# Revit family: IS_iLifeA_T4518_BIM_NL
name_source: partatom
category: Plumbing Fixtures
units: mm (PartAtom-declared; Revit-internal decimal feet)

## family parameters
Always vertical = No
Cut with Voids When Loaded = No
OmniClass Number = 23.45.05.14.14
OmniClass Title = Sinks/Lavatories
Part Type = Normal
Room Calculation Point = No
Round Connector Dimension = Use Diameter
Shared = No
Work Plane-Based = No

## types (1)
- T451801 - I.life A pedestal white - White
    Accessories = https://www.idealstandard.nl
    Afmetingen = 168 x 705 x 185mm
    AfstandsEenheid = Millimeter
    Afwerking = Weiß
    AreaMeasurement = internal
    AreaUnits = Millimeter
    Artikelnummer = T451801
    Artikelomschrijving = I.life A sokkel wit - Wit
    Artikelreferentie = I.life A pedestal white
    Auteur = Ideal Standard
    BIMObjectName = IS_IdealStandard_Pedestalwashbasins_I.life_T4518
    BIMobject category = Other Sanitary
    BIMobject category code = sanitary-sanitary-other
    BIMobject main category = Sanitary
    BIMobject main category code = sanitary
    BarCode = 8014140485865
    Beschrijvinggarantie = Herstellergarantie
    Bestanddelen = Sockel weiß
    BimObjectNaam = IS_IdealStandard_Pedestalwashbasins_I.life_T4518
    Brand url = https://www.idealstandard.nl
    Breedte = 0
    BrutoGewicht = 0
    Color = Weiß
    ConnectionType = Plumbing
    Cost = 0 $
    CurrencyUnit = €
    CurrentRevision = 1
    Date of publishing = 28/06/2021
    Description = I.life A sokkel wit - Wit
    Diepte = 0 mm  [stored 0 ft]
    DrainSize = 0 mm  [stored 0 ft]
    DurationUnit = Years
    DuurEenheid = Jaar
    Edition number = 1
    Eigenschappen = Sockel weiß
    Features = Sockel weiß
    Finish = Weiß
    GTIN code = https://8014140485865
    Garantieonderdelen = 5
    Garantieunits = Jaar
    GrootteAfvoergat = 0
    Help = https://www.idealstandard.nl
    Hoogte = 705.0001
    Hulp = https://www.idealstandard.nl
    IFC Classification = Sanitary Terminal
    IfcExportAs = IfcSanitaryTerminalType
    IfcExportType = PEDESTAL
    Installatieinstructies = https://www.idealstandard.nl
    Installation instructions = https://www.idealstandard.nl
    InstallationInstructions = https://www.idealstandard.nl
    Kleur = Weiß
    Lengte = 168 mm
    LinearUnits = millimeter
    MainColor = Weiß
    MaintenanceInformation = https://www.idealstandard.nl
    Manufacturer = Ideal Standard
    Manufacturer name = Ideal Standard
    ManufacturerURL = https://www.idealstandard.nl
    Material = Vitrous China
    Material main = Vitrous China
    Merk = Ideal Standard
    Model = T451801
    ModelNumber = T451801
    ModelReference = I.life A pedestal white
    Montageinstuctie = Wandhangende wastafels
    NBS Reference Code = 35-79-64
    NBS Reference Description = Pedestal Wash Basins
    Name = Pedestalwashbasins_I.life_T4518_IdealStandard
    NettWeight = 11.74
    Nettogewicht = 0
    NominalDepth = 168 mm
    NominalHeight = 705 mm
    NominalWidth = 185 mm
    Normen = Pedestalwashbasins_I.life_T4518_IdealStandard
    OmniClass Code = 23-21 25 23 15
    OmniClass Description = Pedestals
    Ophangingwastafel = Wandhangende wastafels
    OppervlakteEenheid = millimeter
    Overloop = 0 mm  [stored 0 ft]
    Product Guid = 088b959a-6ddd-48dc-a18d-73adf966bce9
    Product SKU = T4518
    Product certification = https://www.idealstandard.nl
    Product data url = https://bimobject.com
    Product family = I.life
    Product group = Pedestal
    Product name = I.life A pedestal white
    Product url = https://www.idealstandard.nl
    ProductInformation = https://www.idealstandard.nl
    ProductSoort = Wastafel
    Productinformatie = https://www.idealstandard.nl
    QR code = http://bimobject.com
    Referentie = I.life A pedestal white
    Revisie = 1
    Shape = sculpture
    Size = 168 x 705 x 185mm
    Space = Internal
    SpareParts = https://www.idealstandard.nl
    Technical description = https://www.idealstandard.nl
    Telefoonnummer = 077 355 08 08
    Typeconnectie = loodgieter
    Typewastafel = wandhangende wastafel
    URL = https://https:
    Uniclass 1.4 Code = L8443
    Uniclass 1.4 Description = Stands, pedestals
    Uniclass 2.0 Code = PR-35-79-64
    Uniclass 2.0 Description = Pedestal Wash Basins
    Uniclass 2015 Code = Pr_40_20_96_63
    Uniclass 2015 Name = Pedestal wash basins
    Uniclass2015Beschrijving = Pedestal washbasins
    Uniclass2015Code = Pr_40_20_96_63
    Uniclass2015Referentie = Pr_40_20_96_63
    Uniclass2015Title = Pedestal washbasins
    Uniclass2015Version = v1.20
    Urlproducent = https://https:
    ValutaEenheid = €
    Versie = 1
    Version = 1
    Vervangingskosten = 0
    VolumeUnits = liters
    Volumeunits = liters
    Vorm = beeldhouwwerk
    WRASURL = https://www.wrasapprovals.co.uk
    WaarborgGarantieInstallatie = https://www.idealstandard.nl
    WarrantyDescription = manufacturer warranty
    WarrantyDurationParts = 99
    WarrantyDurationUnit = years
    Wisselstukken = https://www.idealstandard.nl
    Youtube clip = https://www.youtube.com

note: [stored X ft] marks values corroborated as IEEE doubles in the binary element streams (Revit-internal decimal feet)

## geometry (parser evidence)
native form markers: Sweep x3
no freeform markers — native parametric forms only
